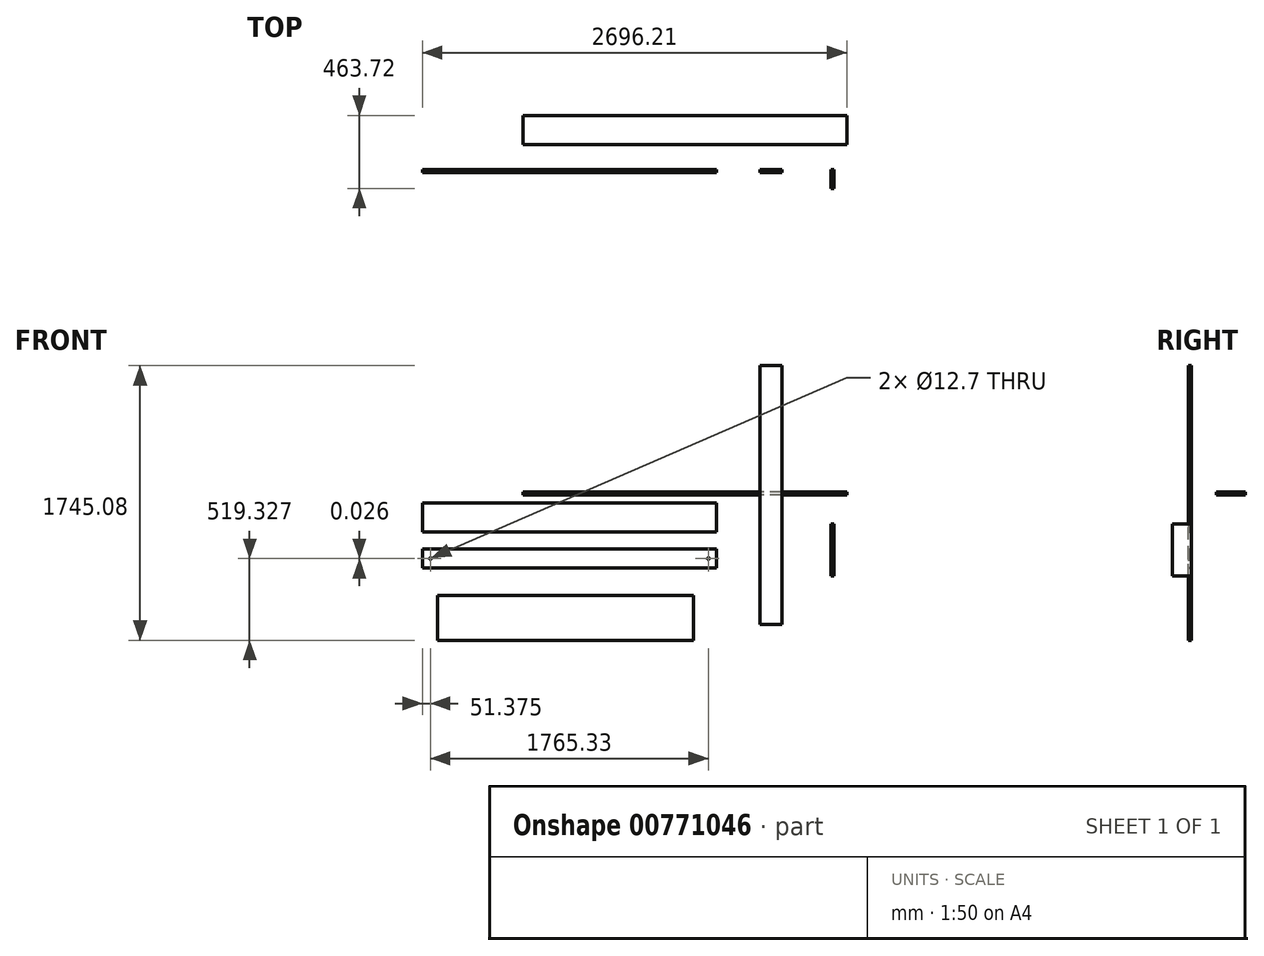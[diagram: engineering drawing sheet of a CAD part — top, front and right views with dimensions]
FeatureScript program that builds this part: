
annotation { "Feature Type Name" : "Feature", "Feature Type Description" : "" }
export const myFeature = defineFeature(function(context is Context, id is Id, definition is map)
    precondition{}
    {
        {
            var Q0;
            Q0=qCreatedBy(makeId("Front.planeOp"),FACE);
            var sketch = newSketch(context, id + "F0", { "sketchPlane" : qUnion([Q0])});
            skLineSegment(sketch, "E0.bottom", {"start": v(69.85, -822.32) * mm, "end": v(-69.85, -822.32) * mm});
            skLineSegment(sketch, "E0.top", {"start": v(69.85, 822.33) * mm, "end": v(-69.85, 822.33) * mm});
            skLineSegment(sketch, "E0.left", {"start": v(69.85, -822.32) * mm, "end": v(69.85, 822.33) * mm});
            skLineSegment(sketch, "E0.right", {"start": v(-69.85, -822.32) * mm, "end": v(-69.85, 822.33) * mm});
            skPoint(sketch, "E0.middle", {"position": v(0, 0) * mm});
            skSolve(sketch);
        }
        {
            var Q0;
            Q0=makeQuery(id+"F0.imprint","IMPRINT",FACE,{"disambiguationData":[TD([[makeQuery(id+"F0.imprint","IMPRINT",EDGE,{"derivedFrom":sQuery(id+"F0.wireOp",EDGE,"E0.bottom")}),-1.0]])]});
            extrude(context, id + "F1", {"entities" : qUnion([Q0]), "depth" : 19.05 * mm, "offsetDistance" : 25.4 * mm});
        }
        {
            var Q0;
            Q0=qCreatedBy(makeId("Top.planeOp"),FACE);
            var sketch = newSketch(context, id + "F2", { "sketchPlane" : qUnion([Q0])});
            skLineSegment(sketch, "E1.bottom", {"start": v(482.85, 158.92) * mm, "end": v(-1574.55, 158.92) * mm});
            skLineSegment(sketch, "E1.top", {"start": v(482.85, 343.07) * mm, "end": v(-1574.55, 343.07) * mm});
            skLineSegment(sketch, "E1.left", {"start": v(482.85, 158.92) * mm, "end": v(482.85, 343.07) * mm});
            skLineSegment(sketch, "E1.right", {"start": v(-1574.55, 158.92) * mm, "end": v(-1574.55, 343.07) * mm});
            skPoint(sketch, "E1.middle", {"position": v(-545.85, 251) * mm});
            skSolve(sketch);
        }
        {
            var Q0;
            Q0=makeQuery(id+"F2.imprint","IMPRINT",FACE,{"disambiguationData":[TD([[makeQuery(id+"F2.imprint","IMPRINT",EDGE,{"derivedFrom":sQuery(id+"F2.wireOp",EDGE,"E1.bottom")}),-1.0]])]});
            extrude(context, id + "F3", {"entities" : qUnion([Q0]), "depth" : 19.05 * mm, "offsetDistance" : 25.4 * mm});
        }
        {
            var Q0;
            Q0=makeQuery(id+"F1.opExtrude","SWEPT_BODY",BODY,{"disambiguationData":[OSD([sQuery(id+"F0.wireOp",EDGE,"E0.bottom"),sQuery(id+"F0.wireOp",EDGE,"E0.top"),sQuery(id+"F0.wireOp",EDGE,"E0.left"),sQuery(id+"F0.wireOp",EDGE,"E0.right")])]});
            transform(context, id + "F4", {"entities" : qUnion([Q0]), "transformType" : TransformType.TRANSLATION_3D, "dx" : -459.74 * mm, "dy" : 0 * mm, "dz" : 0 * mm, "makeCopy" : true});
        }
        {
            var Q0;
            Q0=makeQuery(id+"F4.opPattern","COPY",BODY,{"derivedFrom":makeQuery(id+"F1.opExtrude","SWEPT_BODY",BODY,{"disambiguationData":[OSD([sQuery(id+"F0.wireOp",EDGE,"E0.bottom"),sQuery(id+"F0.wireOp",EDGE,"E0.top"),sQuery(id+"F0.wireOp",EDGE,"E0.left"),sQuery(id+"F0.wireOp",EDGE,"E0.right")])]}),"instanceName":"1"});
            deleteBodies(context, id + "F5", {"entities" : qUnion([Q0])});
        }
        {
            var Q0;
            Q0=qCreatedBy(makeId("Front.planeOp"),FACE);
            var sketch = newSketch(context, id + "F6", { "sketchPlane" : qUnion([Q0])});
            skLineSegment(sketch, "E2.bottom", {"start": v(-2213.36, -49.16) * mm, "end": v(-346.46, -49.16) * mm});
            skLineSegment(sketch, "E2.top", {"start": v(-2213.36, -233.3) * mm, "end": v(-346.46, -233.3) * mm});
            skLineSegment(sketch, "E2.left", {"start": v(-2213.36, -49.16) * mm, "end": v(-2213.36, -233.3) * mm});
            skLineSegment(sketch, "E2.right", {"start": v(-346.46, -49.16) * mm, "end": v(-346.46, -233.3) * mm});
            skSolve(sketch);
        }
        {
            var Q0;
            Q0=qSketchRegion(id+"F6",true);
            extrude(context, id + "F7", {"entities" : qUnion([Q0]), "depth" : 19.05 * mm, "offsetDistance" : 25.4 * mm});
        }
        {
            var Q0;
            Q0=qCreatedBy(makeId("Front.planeOp"),FACE);
            var sketch = newSketch(context, id + "F8", { "sketchPlane" : qUnion([Q0])});
            skLineSegment(sketch, "E3.bottom", {"start": v(-2212.8, -343.1) * mm, "end": v(-345.9, -343.1) * mm});
            skLineSegment(sketch, "E3.top", {"start": v(-2212.8, -463.76) * mm, "end": v(-345.9, -463.76) * mm});
            skLineSegment(sketch, "E3.left", {"start": v(-2212.8, -343.1) * mm, "end": v(-2212.8, -463.76) * mm});
            skLineSegment(sketch, "E3.right", {"start": v(-345.9, -343.1) * mm, "end": v(-345.9, -463.76) * mm});
            skSolve(sketch);
        }
        {
            var Q0;
            Q0=makeQuery(id+"F8.imprint","IMPRINT",FACE,{"disambiguationData":[TD([[makeQuery(id+"F8.imprint","IMPRINT",EDGE,{"derivedFrom":sQuery(id+"F8.wireOp",EDGE,"E3.bottom")}),-1.0]])]});
            extrude(context, id + "F9", {"entities" : qUnion([Q0]), "depth" : 19.05 * mm, "offsetDistance" : 25.4 * mm});
        }
        {
            var Q0;
            Q0=qCreatedBy(makeId("Front.planeOp"),FACE);
            var sketch = newSketch(context, id + "F10", { "sketchPlane" : qUnion([Q0])});
            skLineSegment(sketch, "E4.bottom", {"start": v(381.95, -182.22) * mm, "end": v(401, -182.22) * mm});
            skLineSegment(sketch, "E4.top", {"start": v(381.95, -512.42) * mm, "end": v(401, -512.42) * mm});
            skLineSegment(sketch, "E4.left", {"start": v(381.95, -182.22) * mm, "end": v(381.95, -512.42) * mm});
            skLineSegment(sketch, "E4.right", {"start": v(401, -182.22) * mm, "end": v(401, -512.42) * mm});
            skSolve(sketch);
        }
        {
            var Q0;
            Q0=qSketchRegion(id+"F10",true);
            extrude(context, id + "F11", {"entities" : qUnion([Q0]), "depth" : 120.65 * mm, "offsetDistance" : 25.4 * mm});
        }
        {
            var Q0;
            Q0=makeQuery(id+"F9.opExtrude","CAP_FACE",FACE,{"disambiguationData":[OSD([sQuery(id+"F8.wireOp",EDGE,"E3.bottom"),sQuery(id+"F8.wireOp",EDGE,"E3.top"),sQuery(id+"F8.wireOp",EDGE,"E3.left"),sQuery(id+"F8.wireOp",EDGE,"E3.right")])],"isStart":false});
            var sketch = newSketch(context, id + "F12", { "sketchPlane" : qUnion([Q0])});
            skLineSegment(sketch, "E5", {"start": v(-2212.8, -403.43) * mm, "end": v(-345.9, -403.43) * mm, "construction": true});
            skLineSegment(sketch, "E6", {"start": v(-396.7, -343.1) * mm, "end": v(-396.7, -463.76) * mm, "construction": true});
            skLineSegment(sketch, "E7", {"start": v(-2162, -343.1) * mm, "end": v(-2162, -463.76) * mm, "construction": true});
            skSolve(sketch);
        }
        {
            var Q0;
            Q0=makeQuery(id+"F12.imprint","IMPRINT",FACE,{"disambiguationData":[TD([[makeQuery(id+"F12.imprint","IMPRINT",EDGE,{"derivedFrom":makeQuery(id+"F9.opExtrude","CAP_EDGE",EDGE,{"disambiguationData":[OSD([sQuery(id+"F8.wireOp",EDGE,"E3.bottom")])],"isStart":false})}),-1.0]])]});
            var sketch = newSketch(context, id + "F13", { "sketchPlane" : qUnion([Q0])});
            skPoint(sketch, "E8", {"position": v(-2161.98, -403.4) * mm});
            skPoint(sketch, "E9", {"position": v(-396.66, -403.43) * mm});
            skSolve(sketch);
        }
        {
            var Q0;
            Q0=sQuery(id+"F13.wireOp",VERTEX,"E8");
            var Q1;
            Q1=sQuery(id+"F13.wireOp",VERTEX,"E9");
            var Q2;
            Q2=makeQuery(id+"F9.opExtrude","SWEPT_BODY",BODY,{"disambiguationData":[OSD([sQuery(id+"F8.wireOp",EDGE,"E3.bottom"),sQuery(id+"F8.wireOp",EDGE,"E3.top"),sQuery(id+"F8.wireOp",EDGE,"E3.left"),sQuery(id+"F8.wireOp",EDGE,"E3.right")])]});
            hole(context, id + "F14", {"style" : HoleStyle.SIMPLE, "endStyle" : HoleEndStyle.THROUGH, "holeDiameter" : 12.7 * mm, "majorDiameter" : 6.35 * mm, "isTappedThrough" : true, "tappedDepth" : 12.7 * mm, "tapClearance" : 3, "locations" : qUnion([Q0, Q1]), "scope" : qUnion([Q2])});
        }
        {
            var Q0;
            Q0=qCreatedBy(makeId("Front.planeOp"),FACE);
            var sketch = newSketch(context, id + "F15", { "sketchPlane" : qUnion([Q0])});
            skLineSegment(sketch, "E10.bottom", {"start": v(-2116.58, -637.01) * mm, "end": v(-490.98, -637.01) * mm});
            skLineSegment(sketch, "E10.top", {"start": v(-2116.58, -922.76) * mm, "end": v(-490.98, -922.76) * mm});
            skLineSegment(sketch, "E10.left", {"start": v(-2116.58, -637.01) * mm, "end": v(-2116.58, -922.76) * mm});
            skLineSegment(sketch, "E10.right", {"start": v(-490.98, -637.01) * mm, "end": v(-490.98, -922.76) * mm});
            skSolve(sketch);
        }
        {
            var Q0;
            Q0=qSketchRegion(id+"F15",true);
            extrude(context, id + "F16", {"entities" : qUnion([Q0]), "depth" : 19.05 * mm, "offsetDistance" : 25.4 * mm});
        }
    });
